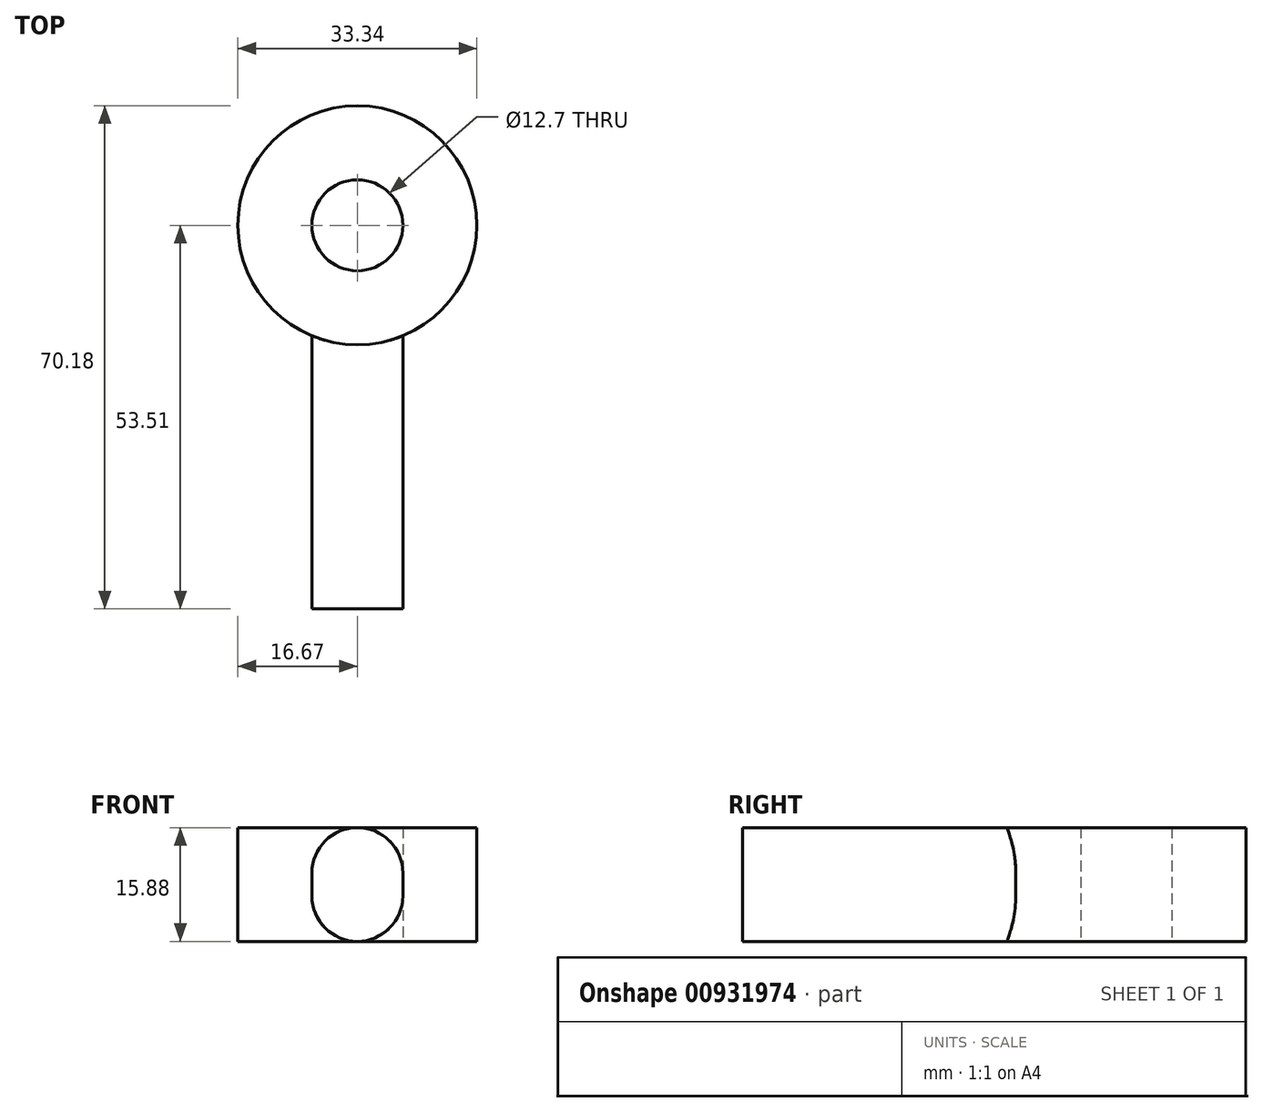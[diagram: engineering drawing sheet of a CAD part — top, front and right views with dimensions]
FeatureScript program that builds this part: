
annotation { "Feature Type Name" : "Feature", "Feature Type Description" : "" }
export const myFeature = defineFeature(function(context is Context, id is Id, definition is map)
    precondition{}
    {
        {
            assignVariable(context, id + "F0", {"name" : "RodEndC", "anyValue" : 15.88 * mm});
        }
        {
            var Q0;
            Q0=qCreatedBy(makeId("Top.planeOp"),FACE);
            var sketch = newSketch(context, id + "F1", { "sketchPlane" : qUnion([Q0])});
            skLineSegment(sketch, "E0", {"start": v(-6.35, -15.41) * mm, "end": v(-6.35, -53.51) * mm});
            skLineSegment(sketch, "E1", {"start": v(-6.35, -53.51) * mm, "end": v(6.35, -53.51) * mm});
            skLineSegment(sketch, "E2", {"start": v(6.35, -53.51) * mm, "end": v(6.35, -15.41) * mm});
            skCircle(sketch, "E3", {"center": v(0, 0) * mm, "radius": 6.35 * mm});
            skArc(sketch, "E4", {"start": v(6.35, -15.41) * mm, "mid": v(0, 16.67) * mm, "end": v(-6.35, -15.41) * mm});
            skSolve(sketch);
        }
        {
            var Q0;
            Q0=makeQuery(id+"F1.imprint","IMPRINT",FACE,{"disambiguationData":[TD([[makeQuery(id+"F1.imprint","IMPRINT",EDGE,{"derivedFrom":sQuery(id+"F1.wireOp",EDGE,"E0")}),1.0]])]});
            extrude(context, id + "F2", {"entities" : qUnion([Q0]), "endBound" : BoundingType.SYMMETRIC, "depth" : getVariable(context, 'RodEndC'), "offsetDistance" : 25.4 * mm});
        }
        {
            var Q0;
            Q0=makeQuery(id+"F2.opExtrude","CAP_EDGE",EDGE,{"disambiguationData":[OSD([sQuery(id+"F1.wireOp",EDGE,"E0")])],"isStart":true});
            var Q1;
            Q1=makeQuery(id+"F2.opExtrude","CAP_EDGE",EDGE,{"disambiguationData":[OSD([sQuery(id+"F1.wireOp",EDGE,"E2")])],"isStart":true});
            var Q2;
            Q2=makeQuery(id+"F2.opExtrude","CAP_EDGE",EDGE,{"disambiguationData":[OSD([sQuery(id+"F1.wireOp",EDGE,"E0")])],"isStart":false});
            var Q3;
            Q3=makeQuery(id+"F2.opExtrude","CAP_EDGE",EDGE,{"disambiguationData":[OSD([sQuery(id+"F1.wireOp",EDGE,"E2")])],"isStart":false});
            fillet(context, id + "F3", {"entities" : qUnion([Q0, Q1, Q2, Q3]), "radius" : 6.35 * mm, "tangentPropagation" : true, "allowEdgeOverflow" : false});
        }
    });
